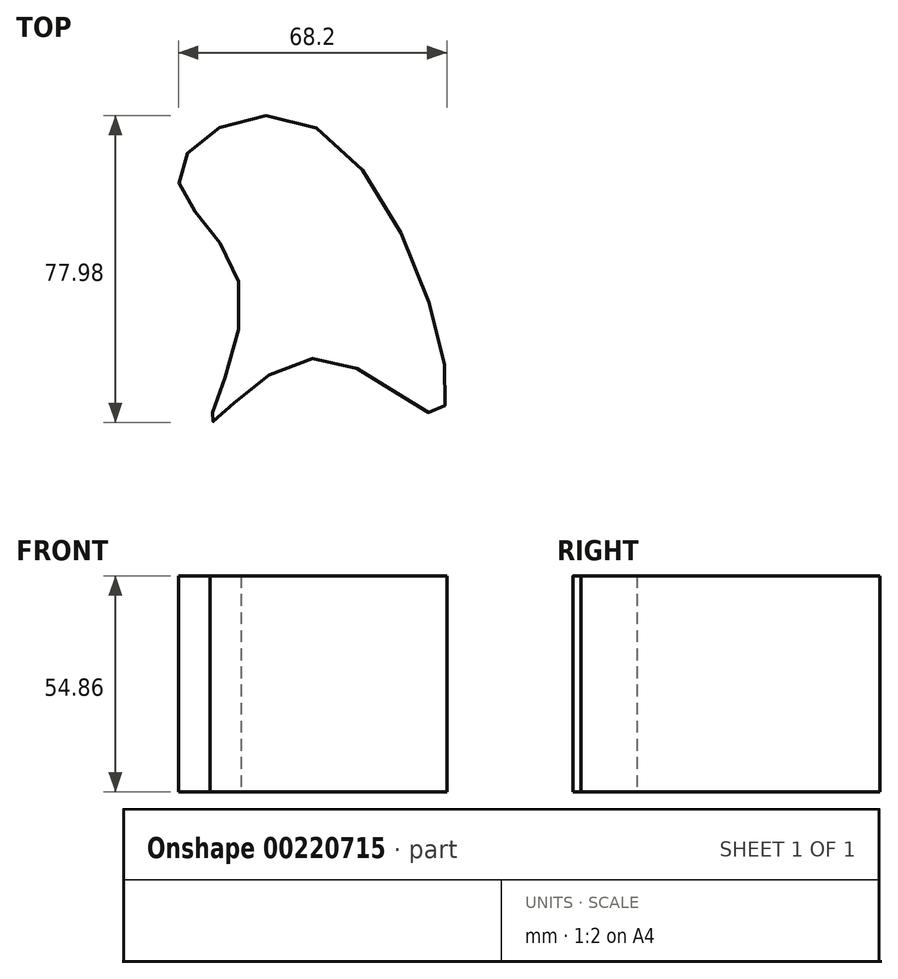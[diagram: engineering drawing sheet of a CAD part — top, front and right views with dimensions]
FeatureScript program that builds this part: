
annotation { "Feature Type Name" : "Feature", "Feature Type Description" : "" }
export const myFeature = defineFeature(function(context is Context, id is Id, definition is map)
    precondition{}
    {
        {
            var Q0;
            Q0=qCreatedBy(makeId("Top.planeOp"),FACE);
            var sketch = newSketch(context, id + "F0", { "sketchPlane" : qUnion([Q0])});
            skFitSpline(sketch, "E0", {"points": [v(0, 40.57) * mm, v(-35.01, 29.09) * mm, v(-19.45, 0) * mm, v(-26.86, -34.27) * mm, v(0, -17.97) * mm, v(31.68, -31.68) * mm, v(0, 40.57) * mm]});
            skSolve(sketch);
        }
        {
            var Q0;
            Q0=makeQuery(id+"F0.imprint","IMPRINT",FACE,{"disambiguationData":[TD([[makeQuery(id+"F0.imprint","IMPRINT",EDGE,{"derivedFrom":sQuery(id+"F0.wireOp",EDGE,"E0")}),1.0]])]});
            extrude(context, id + "F1", {"entities" : qUnion([Q0]), "depth" : 54.86 * mm});
        }
    });
